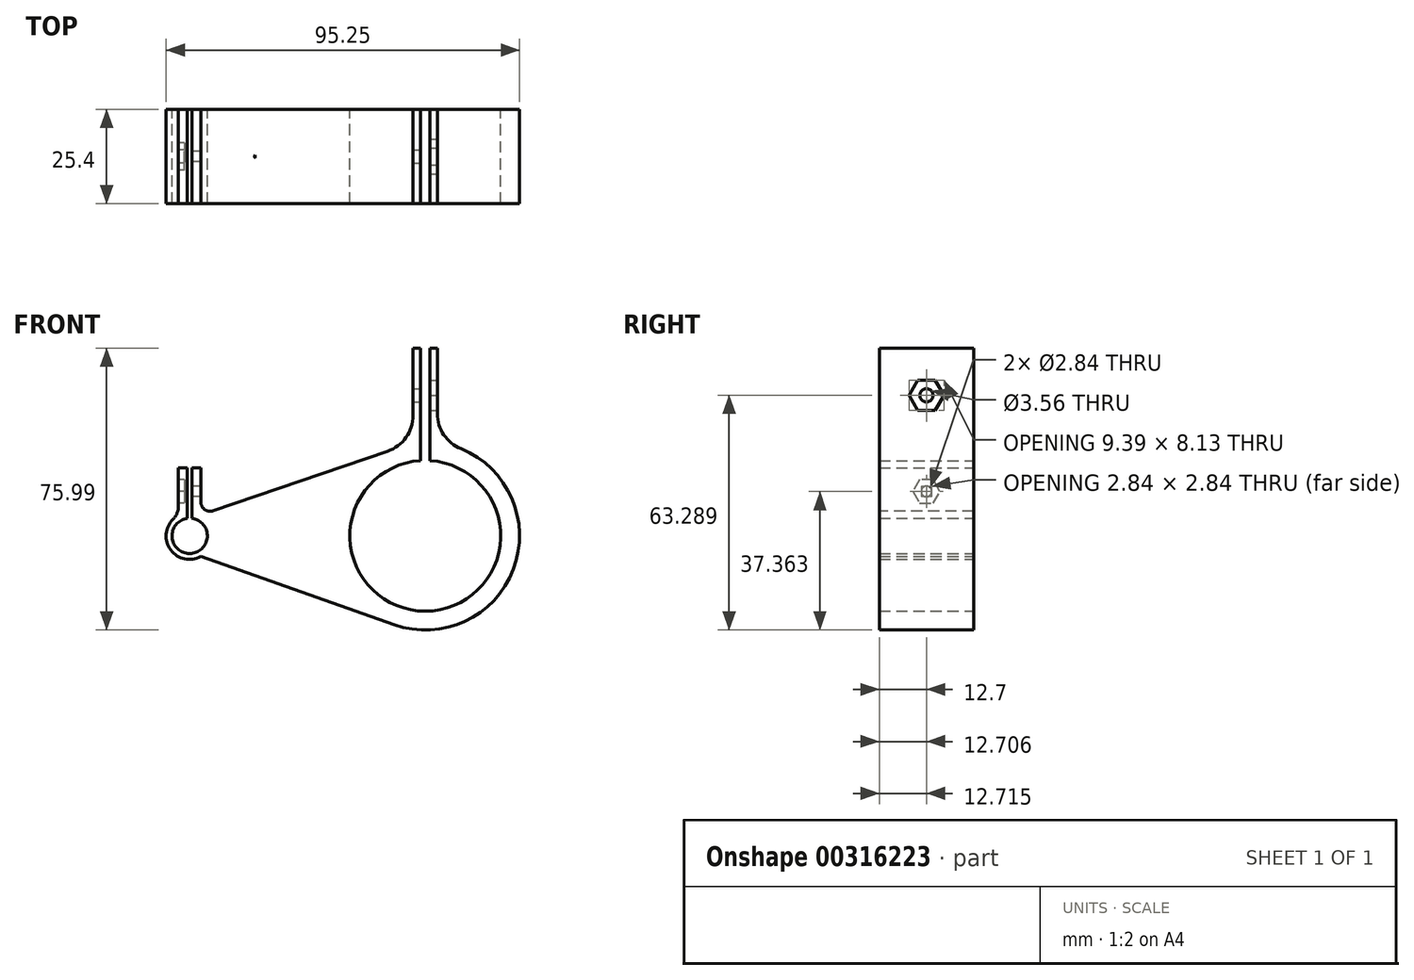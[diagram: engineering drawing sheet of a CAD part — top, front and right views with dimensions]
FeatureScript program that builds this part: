
annotation { "Feature Type Name" : "Feature", "Feature Type Description" : "" }
export const myFeature = defineFeature(function(context is Context, id is Id, definition is map)
    precondition{}
    {
        {
            var Q0;
            Q0=qCreatedBy(makeId("Front.planeOp"),FACE);
            var sketch = newSketch(context, id + "F0", { "sketchPlane" : qUnion([Q0])});
            skArc(sketch, "E0", {"start": v(-3.27, 25.19) * mm, "mid": v(-8.23, 24.03) * mm, "end": v(-12.86, 21.9) * mm});
            skArc(sketch, "E1", {"start": v(-1.27, 20.28) * mm, "mid": v(0, -20.32) * mm, "end": v(1.27, 20.28) * mm});
            skLineSegment(sketch, "E2", {"start": v(-1.27, 25.37) * mm, "end": v(-1.27, 20.28) * mm});
            skLineSegment(sketch, "E3.MirrorCS", {"start": v(1.27, 25.37) * mm, "end": v(1.27, 20.28) * mm});
            skLineSegment(sketch, "E4", {"start": v(-1.27, 25.37) * mm, "end": v(-1.27, 50.59) * mm});
            skLineSegment(sketch, "E5", {"start": v(-1.27, 50.59) * mm, "end": v(-3.27, 50.59) * mm});
            skLineSegment(sketch, "E6", {"start": v(-3.27, 50.59) * mm, "end": v(-3.27, 25.19) * mm});
            skLineSegment(sketch, "E7.MirrorCS", {"start": v(1.27, 25.37) * mm, "end": v(1.27, 50.59) * mm});
            skLineSegment(sketch, "E8.MirrorCS", {"start": v(3.27, 50.59) * mm, "end": v(3.27, 25.19) * mm});
            skLineSegment(sketch, "E9.MirrorCS", {"start": v(1.27, 50.59) * mm, "end": v(3.27, 50.59) * mm});
            skArc(sketch, "E10", {"start": v(-64.14, 4.72) * mm, "mid": v(-63.5, -4.76) * mm, "end": v(-62.87, 4.72) * mm});
            skArc(sketch, "E11", {"start": v(-66.52, 5.59) * mm, "mid": v(-69.09, -3.02) * mm, "end": v(-60.48, -5.59) * mm});
            skLineSegment(sketch, "E12", {"start": v(-63.5, 0) * mm, "end": v(-63.5, 44.67) * mm, "construction": true});
            skLineSegment(sketch, "E13", {"start": v(-64.14, 6.32) * mm, "end": v(-64.14, 4.72) * mm});
            skLineSegment(sketch, "E14.MirrorCS", {"start": v(-62.87, 6.32) * mm, "end": v(-62.87, 4.72) * mm});
            skLineSegment(sketch, "E15", {"start": v(-64.14, 6.32) * mm, "end": v(-64.14, 18.29) * mm});
            skLineSegment(sketch, "E16", {"start": v(-64.14, 18.29) * mm, "end": v(-66.52, 18.29) * mm});
            skLineSegment(sketch, "E17", {"start": v(-66.52, 18.29) * mm, "end": v(-66.52, 5.59) * mm});
            skLineSegment(sketch, "E18.MirrorCS", {"start": v(-62.87, 6.32) * mm, "end": v(-62.87, 18.29) * mm});
            skLineSegment(sketch, "E19.MirrorCS", {"start": v(-60.48, 18.29) * mm, "end": v(-60.48, 5.59) * mm});
            skLineSegment(sketch, "E20.MirrorCS", {"start": v(-62.87, 18.29) * mm, "end": v(-60.48, 18.29) * mm});
            skLineSegment(sketch, "E21", {"start": v(0, 0) * mm, "end": v(-63.5, 0) * mm, "construction": true});
            skLineSegment(sketch, "E22", {"start": v(-60.48, 5.59) * mm, "end": v(-3.27, 25.19) * mm});
            skLineSegment(sketch, "E23", {"start": v(-60.48, -5.59) * mm, "end": v(-3.27, -25.78) * mm});
            skArc(sketch, "E24.trimOffspring", {"start": v(-8.45, -23.95) * mm, "mid": v(24.7, -5.9) * mm, "end": v(3.27, 25.19) * mm});
            skSolve(sketch);
        }
        {
            var Q0;
            Q0=makeQuery(id+"F0.imprint","IMPRINT",FACE,{"disambiguationData":[TD([[makeQuery(id+"F0.imprint","IMPRINT",EDGE,{"derivedFrom":sQuery(id+"F0.wireOp",EDGE,"E1")}),-1.0]])]});
            extrude(context, id + "F1", {"entities" : qUnion([Q0]), "depth" : 25.4 * mm});
        }
        {
            var Q0;
            Q0=makeQuery(id+"F1.opExtrude","SWEPT_FACE",FACE,{"disambiguationData":[OSD([sQuery(id+"F0.wireOp",EDGE,"E8.MirrorCS")])]});
            var sketch = newSketch(context, id + "F2", { "sketchPlane" : qUnion([Q0])});
            skCircle(sketch, "E25.cCircle", {"center": v(-12.7, 37.89) * mm, "radius": 4.06 * mm, "construction": true});
            skLineSegment(sketch, "E25.0", {"start": v(-8, 37.89) * mm, "end": v(-10.35, 33.82) * mm});
            skLineSegment(sketch, "E25.1", {"start": v(-10.35, 33.82) * mm, "end": v(-15.05, 33.82) * mm});
            skLineSegment(sketch, "E25.2", {"start": v(-15.05, 33.82) * mm, "end": v(-17.4, 37.89) * mm});
            skLineSegment(sketch, "E25.3", {"start": v(-17.4, 37.89) * mm, "end": v(-15.05, 41.95) * mm});
            skLineSegment(sketch, "E25.4", {"start": v(-15.05, 41.95) * mm, "end": v(-10.35, 41.95) * mm});
            skLineSegment(sketch, "E25.5", {"start": v(-10.35, 41.95) * mm, "end": v(-8, 37.89) * mm});
            skPoint(sketch, "E25.0.midPoint", {"position": v(-9.18, 35.86) * mm});
            skSolve(sketch);
        }
        {
            var Q0;
            Q0=makeQuery(id+"F2.imprint","IMPRINT",FACE,{"disambiguationData":[TD([[makeQuery(id+"F2.imprint","IMPRINT",EDGE,{"derivedFrom":sQuery(id+"F2.wireOp",EDGE,"E25.0")}),-1.0]])]});
            extrude(context, id + "F3", {"entities" : qUnion([Q0]), "operationType" : NewBodyOperationType.REMOVE, "oppositeDirection" : true, "depth" : 2.78 * mm});
        }
        {
            var Q0;
            Q0=makeQuery(id+"F1.opExtrude","SWEPT_FACE",FACE,{"disambiguationData":[OSD([sQuery(id+"F0.wireOp",EDGE,"E8.MirrorCS")])]});
            var sketch = newSketch(context, id + "F4", { "sketchPlane" : qUnion([Q0])});
            skPoint(sketch, "E26", {"position": v(-12.7, 37.89) * mm});
            skSolve(sketch);
        }
        {
            var Q0;
            Q0=sQuery(id+"F4.wireOp",VERTEX,"E26");
            var Q1;
            Q1=makeQuery(id+"F1.opExtrude","SWEPT_BODY",BODY,{"disambiguationData":[OSD([sQuery(id+"F0.wireOp",EDGE,"E1"),sQuery(id+"F0.wireOp",EDGE,"E2"),sQuery(id+"F0.wireOp",EDGE,"E3.MirrorCS"),sQuery(id+"F0.wireOp",EDGE,"E4"),sQuery(id+"F0.wireOp",EDGE,"E5"),sQuery(id+"F0.wireOp",EDGE,"E6"),sQuery(id+"F0.wireOp",EDGE,"E7.MirrorCS"),sQuery(id+"F0.wireOp",EDGE,"E8.MirrorCS"),sQuery(id+"F0.wireOp",EDGE,"E9.MirrorCS"),sQuery(id+"F0.wireOp",EDGE,"E10"),sQuery(id+"F0.wireOp",EDGE,"E11"),sQuery(id+"F0.wireOp",EDGE,"E13"),sQuery(id+"F0.wireOp",EDGE,"E14.MirrorCS"),sQuery(id+"F0.wireOp",EDGE,"E15"),sQuery(id+"F0.wireOp",EDGE,"E16"),sQuery(id+"F0.wireOp",EDGE,"E17"),sQuery(id+"F0.wireOp",EDGE,"E18.MirrorCS"),sQuery(id+"F0.wireOp",EDGE,"E19.MirrorCS"),sQuery(id+"F0.wireOp",EDGE,"E20.MirrorCS"),sQuery(id+"F0.wireOp",EDGE,"E22"),sQuery(id+"F0.wireOp",EDGE,"E23"),sQuery(id+"F0.wireOp",EDGE,"E24.trimOffspring")])]});
            hole(context, id + "F5", {"style" : HoleStyle.SIMPLE, "endStyle" : HoleEndStyle.THROUGH, "holeDiameter" : 3.56 * mm, "tappedDepth" : 12.7 * mm, "tapClearance" : 3, "locations" : qUnion([Q0]), "scope" : qUnion([Q1])});
        }
        {
            var Q0;
            Q0=makeQuery(id+"F1.opExtrude","SWEPT_FACE",FACE,{"disambiguationData":[OSD([sQuery(id+"F0.wireOp",EDGE,"E17")])]});
            var sketch = newSketch(context, id + "F6", { "sketchPlane" : qUnion([Q0])});
            skCircle(sketch, "E27.cCircle", {"center": v(12.7, 11.94) * mm, "radius": 3.18 * mm, "construction": true});
            skLineSegment(sketch, "E27.0", {"start": v(14.53, 8.76) * mm, "end": v(10.87, 8.76) * mm});
            skLineSegment(sketch, "E27.1", {"start": v(10.87, 8.76) * mm, "end": v(9.03, 11.94) * mm});
            skLineSegment(sketch, "E27.2", {"start": v(9.03, 11.94) * mm, "end": v(10.87, 15.11) * mm});
            skLineSegment(sketch, "E27.3", {"start": v(10.87, 15.11) * mm, "end": v(14.53, 15.11) * mm});
            skLineSegment(sketch, "E27.4", {"start": v(14.53, 15.11) * mm, "end": v(16.37, 11.94) * mm});
            skLineSegment(sketch, "E27.5", {"start": v(16.37, 11.94) * mm, "end": v(14.53, 8.76) * mm});
            skPoint(sketch, "E27.0.midPoint", {"position": v(12.7, 8.76) * mm});
            skSolve(sketch);
        }
        {
            var Q0;
            Q0=makeQuery(id+"F6.imprint","IMPRINT",FACE,{"disambiguationData":[TD([[makeQuery(id+"F6.imprint","IMPRINT",EDGE,{"derivedFrom":sQuery(id+"F6.wireOp",EDGE,"E27.0")}),-1.0]])]});
            extrude(context, id + "F7", {"entities" : qUnion([Q0]), "operationType" : NewBodyOperationType.REMOVE, "oppositeDirection" : true, "depth" : 1.59 * mm});
        }
        {
            var Q0;
            Q0=makeQuery(id+"F7.boolean.opBoolean","COPY",FACE,{"derivedFrom":makeQuery(id+"F7.opExtrude","CAP_FACE",FACE,{"disambiguationData":[OSD([sQuery(id+"F6.wireOp",EDGE,"E27.0"),sQuery(id+"F6.wireOp",EDGE,"E27.1"),sQuery(id+"F6.wireOp",EDGE,"E27.2"),sQuery(id+"F6.wireOp",EDGE,"E27.3"),sQuery(id+"F6.wireOp",EDGE,"E27.4"),sQuery(id+"F6.wireOp",EDGE,"E27.5")])],"isStart":false})});
            var sketch = newSketch(context, id + "F8", { "sketchPlane" : qUnion([Q0])});
            skPoint(sketch, "E28", {"position": v(12.69, 11.96) * mm});
            skSolve(sketch);
        }
        {
            var Q0;
            Q0=makeQuery(id+"F1.opExtrude","SWEPT_EDGE",EDGE,{"disambiguationData":[OSD([sQuery(id+"F0.wireOp",EDGE,"E0"),sQuery(id+"F0.wireOp",EDGE,"E6"),sQuery(id+"F0.wireOp",EDGE,"E22")])]});
            fillet(context, id + "F9", {"entities" : qUnion([Q0]), "radius" : 10.16 * mm, "tangentPropagation" : true, "allowEdgeOverflow" : false});
        }
        {
            var Q0;
            Q0=makeQuery(id+"F1.opExtrude","SWEPT_EDGE",EDGE,{"disambiguationData":[OSD([sQuery(id+"F0.wireOp",EDGE,"E8.MirrorCS"),sQuery(id+"F0.wireOp",EDGE,"E24.trimOffspring")])]});
            fillet(context, id + "F10", {"entities" : qUnion([Q0]), "radius" : 10.16 * mm, "tangentPropagation" : true, "allowEdgeOverflow" : false});
        }
        {
            var Q0;
            Q0=makeQuery(id+"F1.opExtrude","SWEPT_EDGE",EDGE,{"disambiguationData":[OSD([sQuery(id+"F0.wireOp",EDGE,"E19.MirrorCS"),sQuery(id+"F0.wireOp",EDGE,"E22")])]});
            fillet(context, id + "F11", {"entities" : qUnion([Q0]), "radius" : 2.54 * mm, "tangentPropagation" : true, "allowEdgeOverflow" : false});
        }
        {
            var Q0;
            Q0=makeQuery(id+"F1.opExtrude","SWEPT_EDGE",EDGE,{"disambiguationData":[OSD([sQuery(id+"F0.wireOp",EDGE,"E11"),sQuery(id+"F0.wireOp",EDGE,"E17")])]});
            fillet(context, id + "F12", {"entities" : qUnion([Q0]), "radius" : 5.08 * mm, "tangentPropagation" : true, "allowEdgeOverflow" : false});
        }
        {
            var Q0;
            Q0=sQuery(id+"F8.wireOp",VERTEX,"E28");
            var Q1;
            Q1=makeQuery(id+"F1.opExtrude","SWEPT_BODY",BODY,{"disambiguationData":[OSD([sQuery(id+"F0.wireOp",EDGE,"E1"),sQuery(id+"F0.wireOp",EDGE,"E2"),sQuery(id+"F0.wireOp",EDGE,"E3.MirrorCS"),sQuery(id+"F0.wireOp",EDGE,"E4"),sQuery(id+"F0.wireOp",EDGE,"E5"),sQuery(id+"F0.wireOp",EDGE,"E6"),sQuery(id+"F0.wireOp",EDGE,"E7.MirrorCS"),sQuery(id+"F0.wireOp",EDGE,"E8.MirrorCS"),sQuery(id+"F0.wireOp",EDGE,"E9.MirrorCS"),sQuery(id+"F0.wireOp",EDGE,"E10"),sQuery(id+"F0.wireOp",EDGE,"E11"),sQuery(id+"F0.wireOp",EDGE,"E13"),sQuery(id+"F0.wireOp",EDGE,"E14.MirrorCS"),sQuery(id+"F0.wireOp",EDGE,"E15"),sQuery(id+"F0.wireOp",EDGE,"E16"),sQuery(id+"F0.wireOp",EDGE,"E17"),sQuery(id+"F0.wireOp",EDGE,"E18.MirrorCS"),sQuery(id+"F0.wireOp",EDGE,"E19.MirrorCS"),sQuery(id+"F0.wireOp",EDGE,"E20.MirrorCS"),sQuery(id+"F0.wireOp",EDGE,"E22"),sQuery(id+"F0.wireOp",EDGE,"E23"),sQuery(id+"F0.wireOp",EDGE,"E24.trimOffspring")])]});
            hole(context, id + "F13", {"style" : HoleStyle.SIMPLE, "endStyle" : HoleEndStyle.BLIND, "holeDiameter" : 2.84 * mm, "holeDepth" : 19.05 * mm, "tappedDepth" : 12.7 * mm, "tapClearance" : 3, "locations" : qUnion([Q0]), "scope" : qUnion([Q1])});
        }
    });
